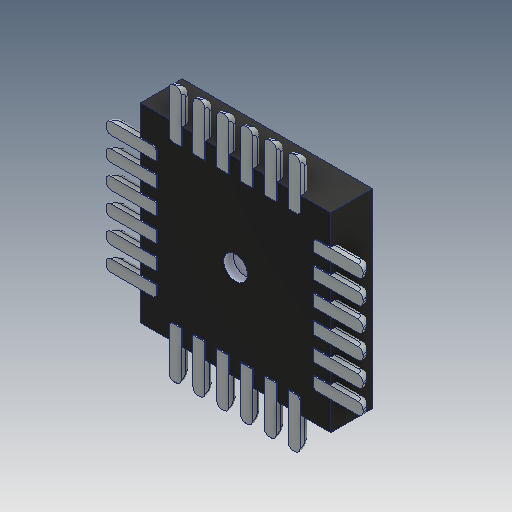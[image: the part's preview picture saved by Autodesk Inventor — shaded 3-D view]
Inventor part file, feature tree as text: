
AUTODESK INVENTOR PART (.ipt)
format: ipt  version: 2018 (Build 220112000, 112)  size: 323,072 bytes
history: native  units: mm
features: fillet x1
ambient origin geometry x8: Origin, YZ Plane, XZ Plane, XY Plane, X Axis, Y Axis, Z Axis, Center Point
bodies: Volumenkörper1 (feature_tree)
feature tree (1):
  fillet  "Fillet3"  [1 undecoded]
note: 1 required parameter value undecoded (feature->parameter linkage not recoverable at this tier; creation-order binding heuristic only, values carry confidence <= 0.55)
